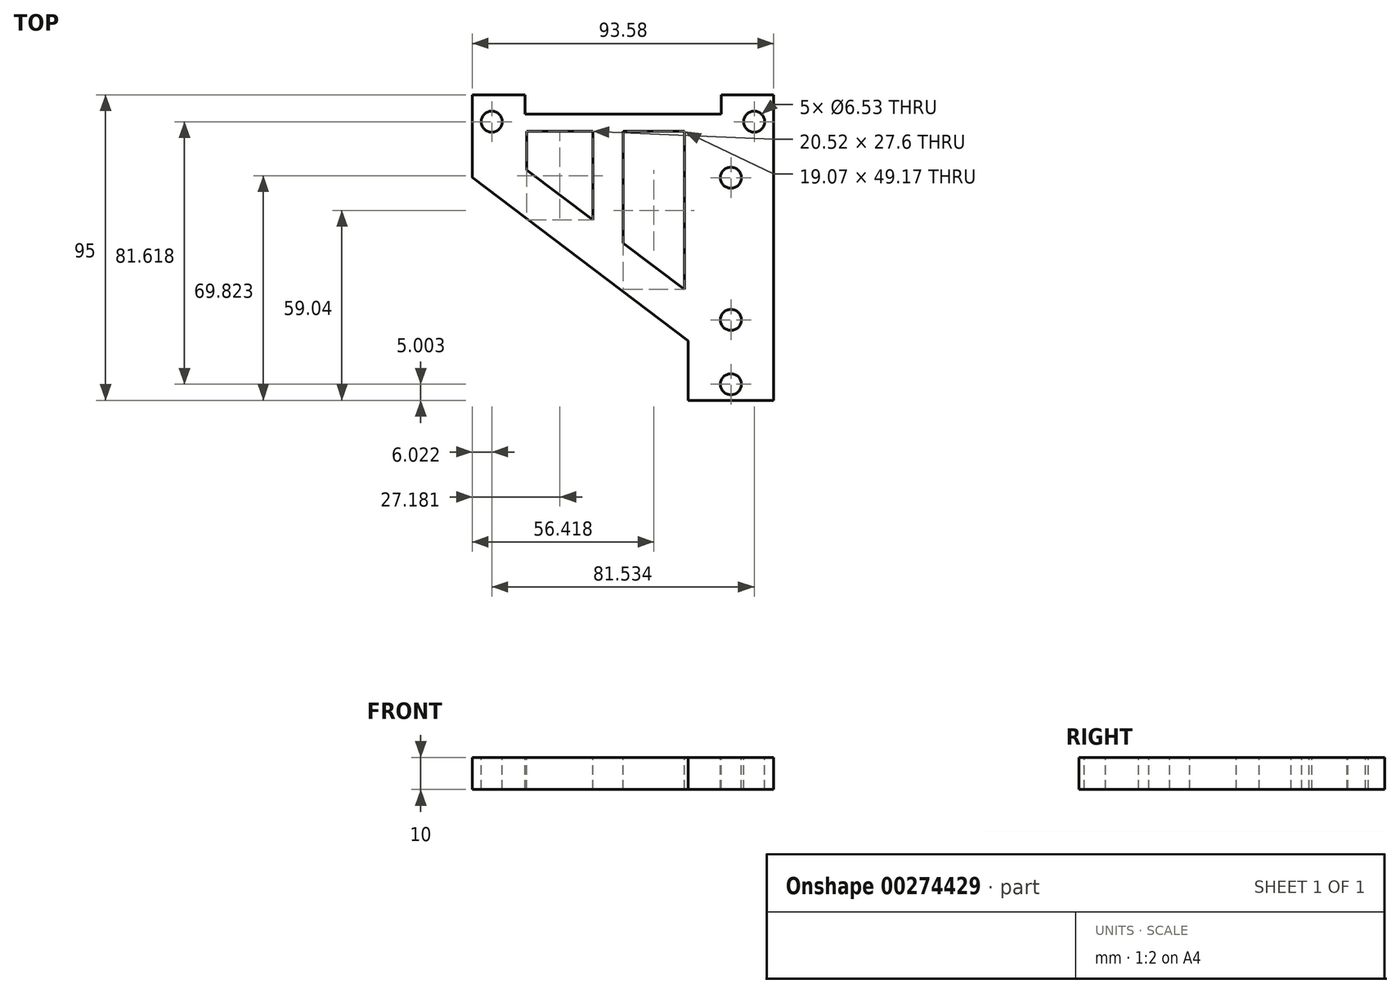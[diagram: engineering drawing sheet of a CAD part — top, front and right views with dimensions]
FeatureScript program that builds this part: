
annotation { "Feature Type Name" : "Feature", "Feature Type Description" : "" }
export const myFeature = defineFeature(function(context is Context, id is Id, definition is map)
    precondition{}
    {
        {
            var Q0;
            Q0=qCreatedBy(makeId("Top.planeOp"),FACE);
            var sketch = newSketch(context, id + "F0", { "sketchPlane" : qUnion([Q0])});
            skLineSegment(sketch, "E0.bottom", {"start": v(-30.52, 46.12) * mm, "end": v(70.06, 46.12) * mm});
            skLineSegment(sketch, "E0.top", {"start": v(-30.52, -51.88) * mm, "end": v(70.06, -51.88) * mm});
            skLineSegment(sketch, "E0.left", {"start": v(-30.52, 46.12) * mm, "end": v(-30.52, -51.88) * mm});
            skLineSegment(sketch, "E0.right", {"start": v(70.06, 46.12) * mm, "end": v(70.06, -51.88) * mm});
            skSolve(sketch);
        }
        {
            var Q0;
            Q0=makeQuery(id+"F0.imprint","IMPRINT",FACE,{"disambiguationData":[TD([[makeQuery(id+"F0.imprint","IMPRINT",EDGE,{"derivedFrom":sQuery(id+"F0.wireOp",EDGE,"E0.bottom")}),-1.0]])]});
            extrude(context, id + "F1", {"entities" : qUnion([Q0]), "depth" : 10 * mm});
        }
        {
            var Q0;
            Q0=makeQuery(id+"F1.opExtrude","CAP_FACE",FACE,{"disambiguationData":[OSD([sQuery(id+"F0.wireOp",EDGE,"E0.bottom"),sQuery(id+"F0.wireOp",EDGE,"E0.top"),sQuery(id+"F0.wireOp",EDGE,"E0.left"),sQuery(id+"F0.wireOp",EDGE,"E0.right")])],"isStart":false});
            var sketch = newSketch(context, id + "F2", { "sketchPlane" : qUnion([Q0])});
            skPoint(sketch, "E1", {"position": v(-21, 37.74) * mm});
            skPoint(sketch, "E2", {"position": v(60.54, 37.74) * mm});
            skSolve(sketch);
        }
        {
            var Q0;
            Q0=sQuery(id+"F2.wireOp",VERTEX,"E1");
            var Q1;
            Q1=sQuery(id+"F2.wireOp",VERTEX,"E2");
            var Q2;
            Q2=makeQuery(id+"F1.opExtrude","SWEPT_BODY",BODY,{"disambiguationData":[OSD([sQuery(id+"F0.wireOp",EDGE,"E0.bottom"),sQuery(id+"F0.wireOp",EDGE,"E0.top"),sQuery(id+"F0.wireOp",EDGE,"E0.left"),sQuery(id+"F0.wireOp",EDGE,"E0.right")])]});
            hole(context, id + "F3", {"style" : HoleStyle.SIMPLE, "endStyle" : HoleEndStyle.THROUGH, "holeDiameter" : 6.53 * mm, "tappedDepth" : 12 * mm, "tapClearance" : 3, "locations" : qUnion([Q0, Q1]), "scope" : qUnion([Q2])});
        }
        {
            var Q0;
            Q0=makeQuery(id+"F1.opExtrude","CAP_FACE",FACE,{"disambiguationData":[OSD([sQuery(id+"F0.wireOp",EDGE,"E0.bottom"),sQuery(id+"F0.wireOp",EDGE,"E0.top"),sQuery(id+"F0.wireOp",EDGE,"E0.left"),sQuery(id+"F0.wireOp",EDGE,"E0.right")])],"isStart":false});
            var sketch = newSketch(context, id + "F4", { "sketchPlane" : qUnion([Q0])});
            skLineSegment(sketch, "E3.bottom", {"start": v(-10.71, 46.12) * mm, "end": v(50.25, 46.12) * mm});
            skLineSegment(sketch, "E3.top", {"start": v(-10.71, 40.12) * mm, "end": v(50.25, 40.12) * mm});
            skLineSegment(sketch, "E3.left", {"start": v(-10.71, 46.12) * mm, "end": v(-10.71, 40.12) * mm});
            skLineSegment(sketch, "E3.right", {"start": v(50.25, 46.12) * mm, "end": v(50.25, 40.12) * mm});
            skSolve(sketch);
        }
        {
            var Q0;
            Q0=makeQuery(id+"F4.imprint","IMPRINT",FACE,{"disambiguationData":[TD([[makeQuery(id+"F4.imprint","IMPRINT",EDGE,{"derivedFrom":sQuery(id+"F4.wireOp",EDGE,"E3.bottom")}),-1.0]])]});
            extrude(context, id + "F5", {"entities" : qUnion([Q0]), "operationType" : NewBodyOperationType.REMOVE, "endBound" : BoundingType.UP_TO_NEXT, "oppositeDirection" : true, "depth" : 25 * mm});
        }
        {
            var Q0;
            Q0=makeQuery(id+"F1.opExtrude","CAP_FACE",FACE,{"disambiguationData":[OSD([sQuery(id+"F0.wireOp",EDGE,"E0.bottom"),sQuery(id+"F0.wireOp",EDGE,"E0.top"),sQuery(id+"F0.wireOp",EDGE,"E0.left"),sQuery(id+"F0.wireOp",EDGE,"E0.right")])],"isStart":false});
            var sketch = newSketch(context, id + "F6", { "sketchPlane" : qUnion([Q0])});
            skLineSegment(sketch, "E4", {"start": v(40.06, -51.88) * mm, "end": v(40.06, -30.33) * mm});
            skLineSegment(sketch, "E5", {"start": v(40.06, -30.33) * mm, "end": v(-30.52, 23.07) * mm});
            skSolve(sketch);
        }
        {
            var Q0;
            {var subQ0=sQuery(id+"F6.wireOp",EDGE,"E4");Q0=makeQuery(id+"F6.imprint","IMPRINT",FACE,{"disambiguationData":[TD([[makeQuery(id+"F6.imprint","IMPRINT",EDGE,{"derivedFrom":subQ0}),1.0]])]});}
            extrude(context, id + "F7", {"entities" : qUnion([Q0]), "operationType" : NewBodyOperationType.REMOVE, "endBound" : BoundingType.UP_TO_NEXT, "oppositeDirection" : true, "depth" : 25 * mm});
        }
        {
            var Q0;
            Q0=makeQuery(id+"F1.opExtrude","CAP_FACE",FACE,{"disambiguationData":[OSD([sQuery(id+"F0.wireOp",EDGE,"E0.bottom"),sQuery(id+"F0.wireOp",EDGE,"E0.top"),sQuery(id+"F0.wireOp",EDGE,"E0.left"),sQuery(id+"F0.wireOp",EDGE,"E0.right")])],"isStart":false});
            var sketch = newSketch(context, id + "F8", { "sketchPlane" : qUnion([Q0])});
            skPoint(sketch, "E6", {"position": v(53.31, -43.88) * mm});
            skPoint(sketch, "E7", {"position": v(53.31, 20.32) * mm});
            skPoint(sketch, "E8", {"position": v(53.31, -23.88) * mm});
            skSolve(sketch);
        }
        {
            var Q0;
            {var subQ2=sQuery(id+"F0.wireOp",EDGE,"E0.right");Q0=makeQuery(id+"F8.imprint","IMPRINT",FACE,{"disambiguationData":[TD([[makeQuery(id+"F8.imprint","IMPRINT",EDGE,{"derivedFrom":makeQuery(id+"F1.opExtrude","CAP_EDGE",EDGE,{"disambiguationData":[OSD([subQ2])],"isStart":false})}),-1.0]])]});}
            var sketch = newSketch(context, id + "F9", { "sketchPlane" : qUnion([Q0])});
            skLineSegment(sketch, "E9", {"start": v(-27.02, 20.42) * mm, "end": v(-27.02, 46.12) * mm});
            skLineSegment(sketch, "E10.bottom", {"start": v(70.06, 46.12) * mm, "end": v(66.56, 46.12) * mm});
            skLineSegment(sketch, "E10.top", {"start": v(70.06, -51.88) * mm, "end": v(66.56, -51.88) * mm});
            skLineSegment(sketch, "E10.left", {"start": v(70.06, 46.12) * mm, "end": v(70.06, -51.88) * mm});
            skLineSegment(sketch, "E10.right", {"start": v(66.56, 46.12) * mm, "end": v(66.56, -51.88) * mm});
            skSolve(sketch);
        }
        {
            var Q0;
            {var subQ0=sQuery(id+"F9.wireOp",EDGE,"E9");Q0=makeQuery(id+"F9.imprint","IMPRINT",FACE,{"disambiguationData":[TD([[makeQuery(id+"F9.imprint","IMPRINT",EDGE,{"derivedFrom":subQ0}),1.0]])]});}
            extrude(context, id + "F10", {"entities" : qUnion([Q0]), "operationType" : NewBodyOperationType.REMOVE, "endBound" : BoundingType.UP_TO_NEXT, "oppositeDirection" : true, "depth" : 25 * mm});
        }
        {
            var Q0;
            Q0 = qSketchRegion(id + "F9", true);
            extrude(context, id + "F11", {"entities" : qUnion([Q0]), "operationType" : NewBodyOperationType.REMOVE, "endBound" : BoundingType.UP_TO_NEXT, "oppositeDirection" : true, "depth" : 25 * mm});
        }
        {
            var Q0;
            Q0=sQuery(id+"F8.wireOp",VERTEX,"E7");
            var Q1;
            Q1=sQuery(id+"F8.wireOp",VERTEX,"E6");
            var Q2;
            Q2=sQuery(id+"F8.wireOp",VERTEX,"E8");
            var Q3;
            Q3=makeQuery(id+"F1.opExtrude","SWEPT_BODY",BODY,{"disambiguationData":[OSD([sQuery(id+"F0.wireOp",EDGE,"E0.bottom"),sQuery(id+"F0.wireOp",EDGE,"E0.top"),sQuery(id+"F0.wireOp",EDGE,"E0.left"),sQuery(id+"F0.wireOp",EDGE,"E0.right")])]});
            hole(context, id + "F12", {"style" : HoleStyle.SIMPLE, "endStyle" : HoleEndStyle.THROUGH, "holeDiameter" : 6.53 * mm, "tappedDepth" : 12 * mm, "tapClearance" : 3, "locations" : qUnion([Q0, Q1, Q2]), "scope" : qUnion([Q3])});
        }
        {
            var Q0;
            {var subQ15=sQuery(id+"F9.wireOp",EDGE,"E9");Q0=makeQuery(id+"F9.imprint","IMPRINT",FACE,{"disambiguationData":[TD([[makeQuery(id+"F9.imprint","IMPRINT",EDGE,{"derivedFrom":subQ15}),-1.0]])]});}
            var sketch = newSketch(context, id + "F13", { "sketchPlane" : qUnion([Q0])});
            skLineSegment(sketch, "E11.bottom", {"start": v(40.06, -51.88) * mm, "end": v(66.56, -51.88) * mm});
            skLineSegment(sketch, "E11.top", {"start": v(40.06, -48.88) * mm, "end": v(66.56, -48.88) * mm});
            skLineSegment(sketch, "E11.left", {"start": v(40.06, -51.88) * mm, "end": v(40.06, -48.88) * mm});
            skLineSegment(sketch, "E11.right", {"start": v(66.56, -51.88) * mm, "end": v(66.56, -48.88) * mm});
            skSolve(sketch);
        }
        {
            var Q0;
            Q0 = qSketchRegion(id + "F13", true);
            extrude(context, id + "F14", {"entities" : qUnion([Q0]), "operationType" : NewBodyOperationType.REMOVE, "endBound" : BoundingType.UP_TO_NEXT, "oppositeDirection" : true, "depth" : 25 * mm});
        }
        {
            var Q0;
            {var subQ15=sQuery(id+"F9.wireOp",EDGE,"E9");Q0=makeQuery(id+"F9.imprint","IMPRINT",FACE,{"disambiguationData":[TD([[makeQuery(id+"F9.imprint","IMPRINT",EDGE,{"derivedFrom":subQ15}),-1.0]])]});}
            var sketch = newSketch(context, id + "F15", { "sketchPlane" : qUnion([Q0])});
            skLineSegment(sketch, "E12", {"start": v(-10.1, 34.74) * mm, "end": v(-10.1, 22.67) * mm});
            skLineSegment(sketch, "E13", {"start": v(-10.1, 22.67) * mm, "end": v(10.42, 7.14) * mm});
            skLineSegment(sketch, "E14", {"start": v(10.42, 7.14) * mm, "end": v(10.42, 34.74) * mm});
            skLineSegment(sketch, "E15", {"start": v(10.42, 34.74) * mm, "end": v(-10.1, 34.74) * mm});
            skLineSegment(sketch, "E16", {"start": v(19.87, 34.74) * mm, "end": v(19.87, 0) * mm});
            skLineSegment(sketch, "E17", {"start": v(19.87, 0) * mm, "end": v(38.93, -14.42) * mm});
            skLineSegment(sketch, "E18", {"start": v(38.93, -14.42) * mm, "end": v(38.93, 34.74) * mm});
            skLineSegment(sketch, "E19", {"start": v(38.93, 34.74) * mm, "end": v(19.87, 34.74) * mm});
            skSolve(sketch);
        }
        {
            var Q0;
            Q0 = qSketchRegion(id + "F15", true);
            extrude(context, id + "F16", {"entities" : qUnion([Q0]), "operationType" : NewBodyOperationType.REMOVE, "endBound" : BoundingType.UP_TO_NEXT, "oppositeDirection" : true, "depth" : 25 * mm});
        }
    });
